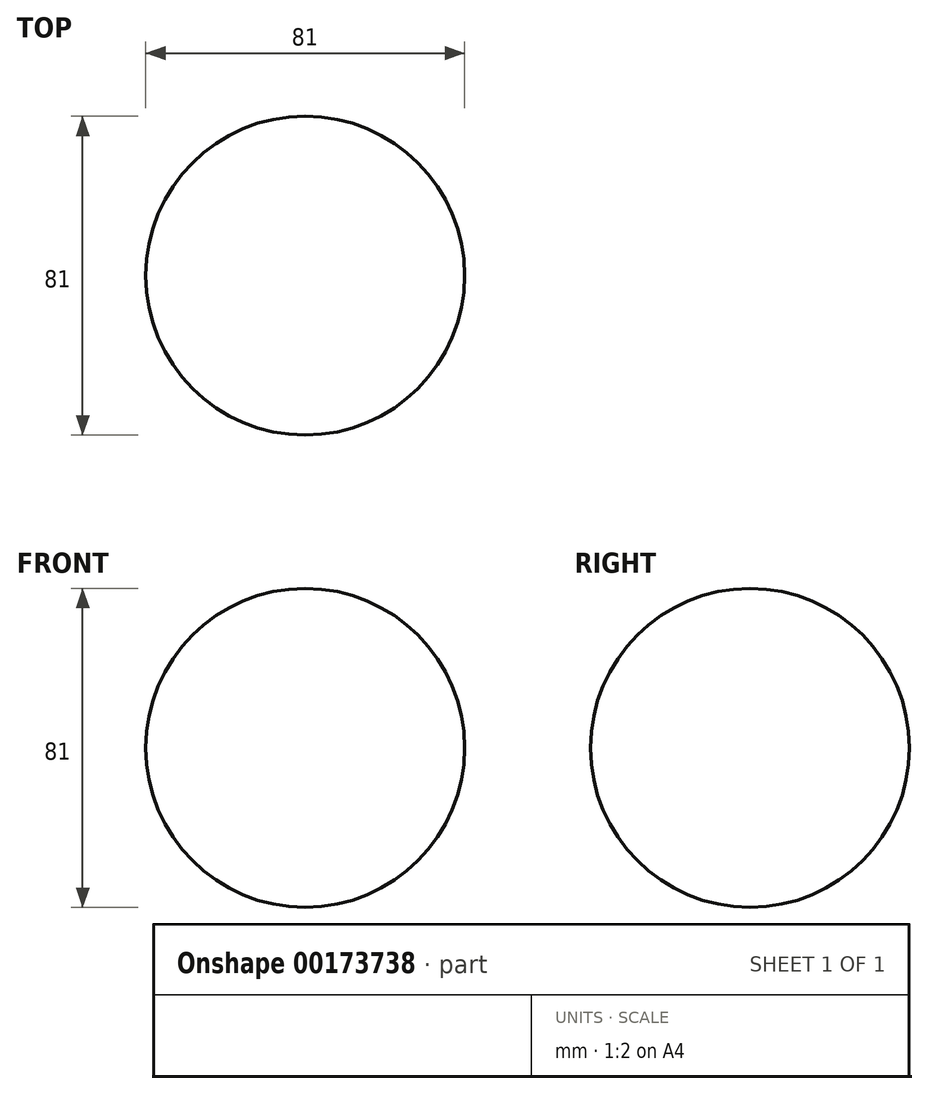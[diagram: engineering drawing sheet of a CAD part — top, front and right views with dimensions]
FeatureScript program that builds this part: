
annotation { "Feature Type Name" : "Feature", "Feature Type Description" : "" }
export const myFeature = defineFeature(function(context is Context, id is Id, definition is map)
    precondition{}
    {
        {
            var Q0;
            Q0=qCreatedBy(makeId("Front.planeOp"),FACE);
            var sketch = newSketch(context, id + "F0", { "sketchPlane" : qUnion([Q0])});
            skArc(sketch, "E0", {"start": v(0, 40.5) * mm, "mid": v(-40.5, 0) * mm, "end": v(0, -40.5) * mm});
            skLineSegment(sketch, "E1", {"start": v(0, 40.5) * mm, "end": v(0, -40.5) * mm});
            skSolve(sketch);
        }
        {
            var Q0;
            Q0=makeQuery(id+"F0.imprint","IMPRINT",FACE,{"disambiguationData":[TD([[makeQuery(id+"F0.imprint","IMPRINT",EDGE,{"derivedFrom":sQuery(id+"F0.wireOp",EDGE,"E0")}),1.0]])]});
            var Q1;
            Q1=sQuery(id+"F0.wireOp",EDGE,"E1");
            revolve(context, id + "F1", {"entities" : qUnion([Q0]), "axis" : qUnion([Q1]), "revolveType" : RevolveType.FULL});
        }
    });
